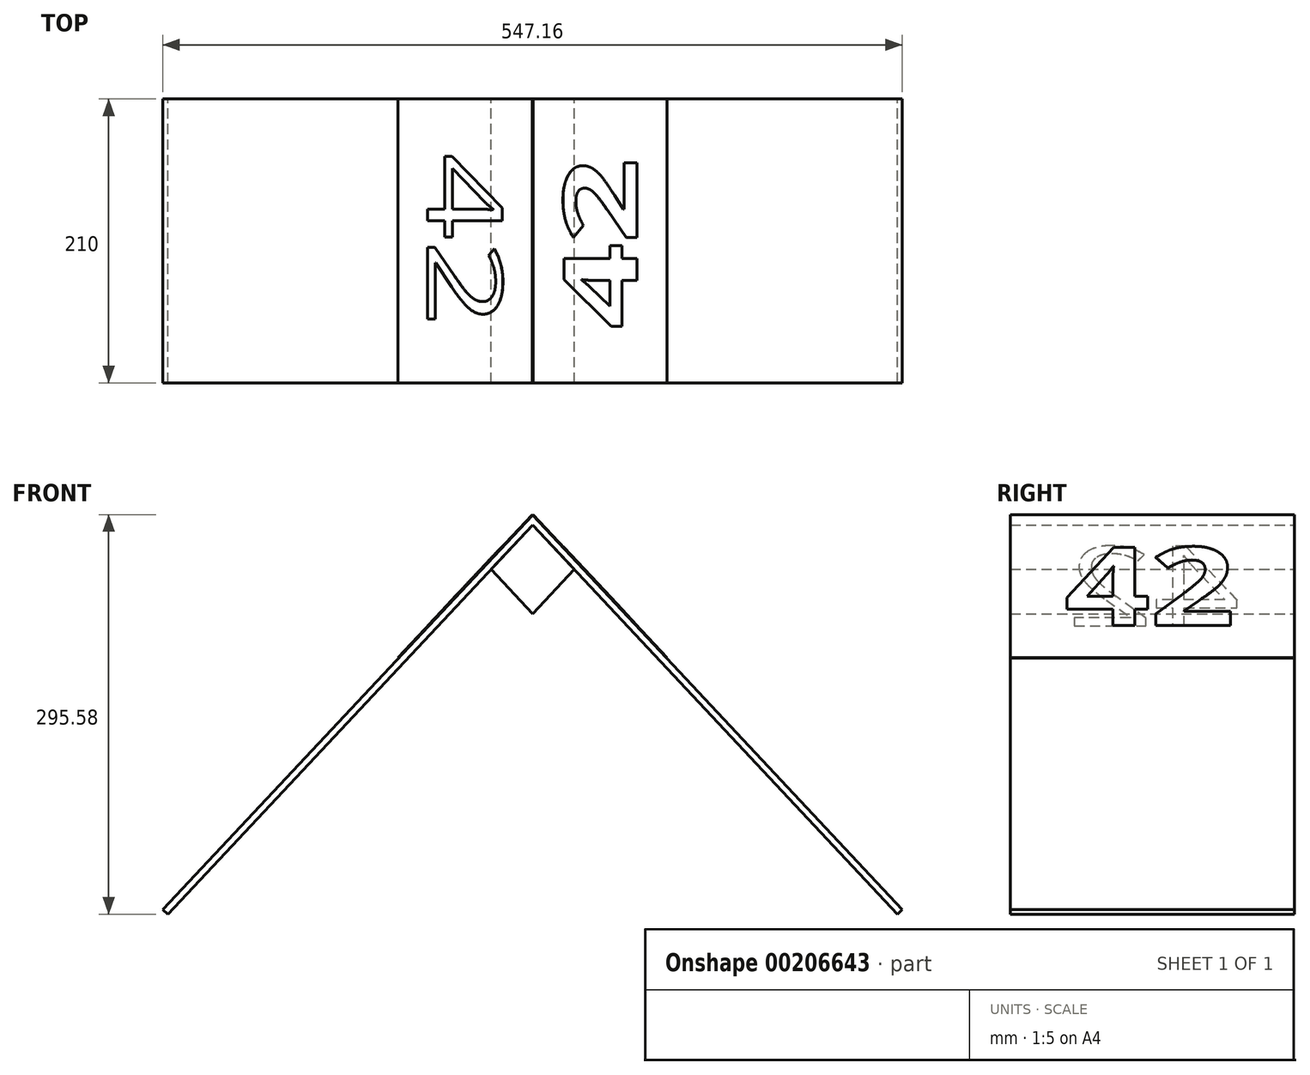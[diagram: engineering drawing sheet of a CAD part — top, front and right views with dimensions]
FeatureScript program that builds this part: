
annotation { "Feature Type Name" : "Feature", "Feature Type Description" : "" }
export const myFeature = defineFeature(function(context is Context, id is Id, definition is map)
    precondition{}
    {
        {
            var Q0;
            Q0=qCreatedBy(makeId("Front.planeOp"),FACE);
            var sketch = newSketch(context, id + "F0", { "sketchPlane" : qUnion([Q0])});
            skLineSegment(sketch, "E0", {"start": v(-273.58, 3.42) * mm, "end": v(-269.93, 0) * mm});
            skLineSegment(sketch, "E1", {"start": v(-269.93, 0) * mm, "end": v(0, 287.92) * mm});
            skLineSegment(sketch, "E2", {"start": v(0, 287.92) * mm, "end": v(269.93, 0) * mm});
            skLineSegment(sketch, "E3", {"start": v(269.93, 0) * mm, "end": v(273.58, 3.42) * mm});
            skLineSegment(sketch, "E4", {"start": v(273.58, 3.42) * mm, "end": v(0, 295.23) * mm});
            skLineSegment(sketch, "E5", {"start": v(0, 295.23) * mm, "end": v(-273.58, 3.42) * mm});
            skLineSegment(sketch, "E6", {"start": v(0, 0) * mm, "end": v(0, 91.1) * mm, "construction": true});
            skSolve(sketch);
        }
        {
            var Q0;
            Q0 = qSketchRegion(id + "F0", true);
            extrude(context, id + "F1", {"entities" : qUnion([Q0]), "depth" : 210 * mm});
        }
        {
            var Q0;
            Q0=qCreatedBy(makeId("Front.planeOp"),FACE);
            var sketch = newSketch(context, id + "F2", { "sketchPlane" : qUnion([Q0])});
            skLineSegment(sketch, "E7", {"start": v(0, 287.92) * mm, "end": v(30.78, 255.1) * mm});
            skLineSegment(sketch, "E8", {"start": v(30.78, 255.1) * mm, "end": v(0, 222.27) * mm});
            skLineSegment(sketch, "E9", {"start": v(0, 222.27) * mm, "end": v(-30.78, 255.1) * mm});
            skLineSegment(sketch, "E10", {"start": v(-30.78, 255.1) * mm, "end": v(0, 287.92) * mm});
            skSolve(sketch);
        }
        {
            var Q0;
            Q0 = qSketchRegion(id + "F2", true);
            var Q1;
            Q1=makeQuery(id+"F1.opExtrude","CAP_FACE",FACE,{"disambiguationData":[OSD([sQuery(id+"F0.wireOp",EDGE,"E0"),sQuery(id+"F0.wireOp",EDGE,"E1"),sQuery(id+"F0.wireOp",EDGE,"E2"),sQuery(id+"F0.wireOp",EDGE,"E3"),sQuery(id+"F0.wireOp",EDGE,"E4"),sQuery(id+"F0.wireOp",EDGE,"E5")])],"isStart":false});
            extrude(context, id + "F3", {"entities" : qUnion([Q0]), "endBound" : BoundingType.UP_TO_SURFACE, "endBoundEntityFace" : qUnion([Q1]), "depth" : 25 * mm});
        }
        {
            var Q0;
            Q0=makeQuery(id+"F1.opExtrude","SWEPT_FACE",FACE,{"disambiguationData":[OSD([sQuery(id+"F0.wireOp",EDGE,"E4")])]});
            var sketch = newSketch(context, id + "F4", { "sketchPlane" : qUnion([Q0])});
            skLineSegment(sketch, "E11.bottom", {"start": v(-210, 215.38) * mm, "end": v(0, 215.38) * mm});
            skLineSegment(sketch, "E11.top", {"start": v(-210, 70.38) * mm, "end": v(0, 70.38) * mm});
            skLineSegment(sketch, "E11.left", {"start": v(-210, 215.38) * mm, "end": v(-210, 70.38) * mm});
            skLineSegment(sketch, "E11.right", {"start": v(0, 215.38) * mm, "end": v(0, 70.38) * mm});
            skSolve(sketch);
        }
        {
            var Q0;
            Q0 = qSketchRegion(id + "F4", true);
            extrude(context, id + "F5", {"entities" : qUnion([Q0]), "depth" : 0.5 * mm});
        }
        {
            var Q0;
            Q0=makeQuery(id+"F1.opExtrude","SWEPT_FACE",FACE,{"disambiguationData":[OSD([sQuery(id+"F0.wireOp",EDGE,"E5")])]});
            var sketch = newSketch(context, id + "F6", { "sketchPlane" : qUnion([Q0])});
            skLineSegment(sketch, "E12.bottom", {"start": v(210, 70.38) * mm, "end": v(0, 70.38) * mm});
            skLineSegment(sketch, "E12.top", {"start": v(210, 215.38) * mm, "end": v(0, 215.38) * mm});
            skLineSegment(sketch, "E12.left", {"start": v(210, 70.38) * mm, "end": v(210, 215.38) * mm});
            skLineSegment(sketch, "E12.right", {"start": v(0, 70.38) * mm, "end": v(0, 215.38) * mm});
            skSolve(sketch);
        }
        {
            var Q0;
            Q0 = qSketchRegion(id + "F6", true);
            extrude(context, id + "F7", {"entities" : qUnion([Q0]), "depth" : .5 * mm});
        }
        {
            var Q0;
            Q0=makeQuery(id+"F5.opExtrude","CAP_FACE",FACE,{"disambiguationData":[OSD([sQuery(id+"F4.wireOp",EDGE,"E11.bottom"),sQuery(id+"F4.wireOp",EDGE,"E11.top"),sQuery(id+"F4.wireOp",EDGE,"E11.left"),sQuery(id+"F4.wireOp",EDGE,"E11.right")])],"isStart":false});
            var sketch = newSketch(context, id + "F8", { "sketchPlane" : qUnion([Q0])});
            skText(sketch, "E13", { "text": "42", "fontName": "OpenSans-Bold.ttf"});
            skLineSegment(sketch, "E14", {"start": v(-105, 70.38) * mm, "end": v(-105, 103.04) * mm, "construction": true});
            skLineSegment(sketch, "E15", {"start": v(0, 142.88) * mm, "end": v(-40, 142.88) * mm, "construction": true});
            const initialGuessF8  = {"E13": [-0.17, 0.10304, 1, 0, 0.07968]};
            skSetInitialGuess(sketch, initialGuessF8);
            skSolve(sketch);
        }
        {
            var Q0;
            Q0 = qSketchRegion(id + "F8", true);
            extrude(context, id + "F9", {"entities" : qUnion([Q0]), "depth" : .1 * mm});
        }
        {
            var Q0;
            Q0=makeQuery(id+"F7.opExtrude","CAP_FACE",FACE,{"disambiguationData":[OSD([sQuery(id+"F6.wireOp",EDGE,"E12.bottom"),sQuery(id+"F6.wireOp",EDGE,"E12.top"),sQuery(id+"F6.wireOp",EDGE,"E12.left"),sQuery(id+"F6.wireOp",EDGE,"E12.right")])],"isStart":false});
            var sketch = newSketch(context, id + "F10", { "sketchPlane" : qUnion([Q0])});
            skText(sketch, "E16", { "text": "42", "fontName": "OpenSans-Regular.ttf"});
            skLineSegment(sketch, "E17", {"start": v(170, 142.88) * mm, "end": v(210, 142.88) * mm, "construction": true});
            skLineSegment(sketch, "E18", {"start": v(105, 70.38) * mm, "end": v(105, 102.35) * mm, "construction": true});
            const initialGuessF10  = {"E16": [0.04, 0.10235, 1, 0, 0.08106]};
            skSetInitialGuess(sketch, initialGuessF10);
            skSolve(sketch);
        }
        {
            var Q0;
            Q0 = qSketchRegion(id + "F10", true);
            extrude(context, id + "F11", {"entities" : qUnion([Q0]), "depth" : .1 * mm});
        }
    });
